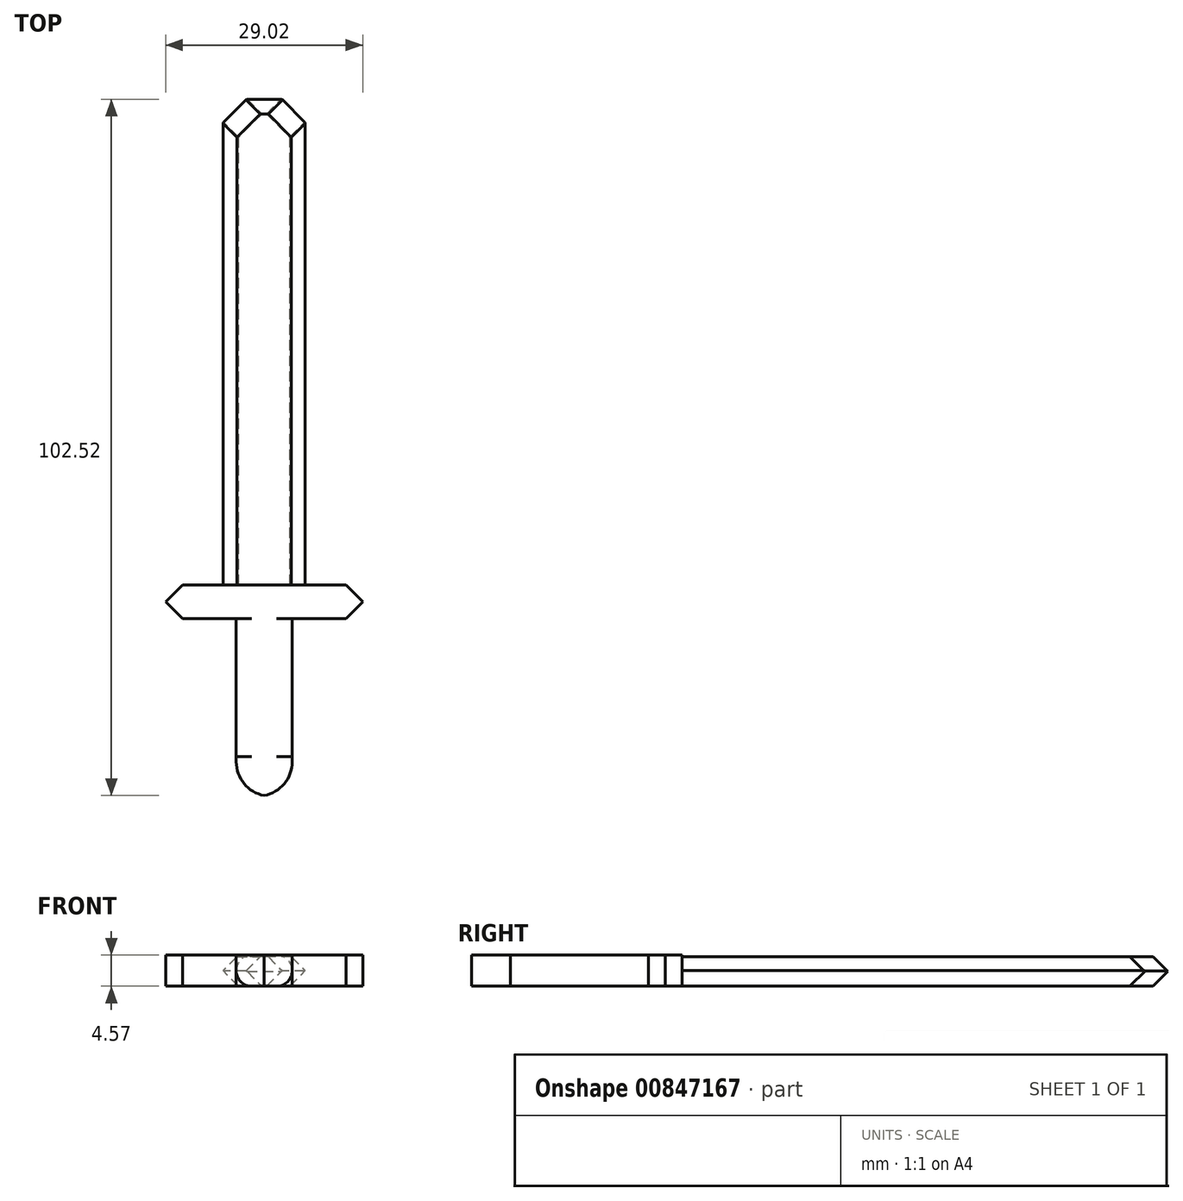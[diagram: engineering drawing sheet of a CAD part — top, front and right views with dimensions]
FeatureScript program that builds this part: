
annotation { "Feature Type Name" : "Feature", "Feature Type Description" : "" }
export const myFeature = defineFeature(function(context is Context, id is Id, definition is map)
    precondition{}
    {
        {
            var Q0;
            Q0=qCreatedBy(makeId("Top.planeOp"),FACE);
            var sketch = newSketch(context, id + "F0", { "sketchPlane" : qUnion([Q0])});
            skLineSegment(sketch, "E0.bottom", {"start": v(6.04, 35.82) * mm, "end": v(-6.04, 35.82) * mm});
            skLineSegment(sketch, "E0.top", {"start": v(6.04, -35.82) * mm, "end": v(-6.04, -35.82) * mm});
            skLineSegment(sketch, "E0.left", {"start": v(6.04, 35.82) * mm, "end": v(6.04, -35.82) * mm});
            skLineSegment(sketch, "E0.right", {"start": v(-6.04, 35.82) * mm, "end": v(-6.04, -35.82) * mm});
            skPoint(sketch, "E0.middle", {"position": v(0, 0) * mm});
            skSolve(sketch);
        }
        {
            var Q0;
            Q0=makeQuery(id+"F0.imprint","IMPRINT",FACE,{"disambiguationData":[TD([[makeQuery(id+"F0.imprint","IMPRINT",EDGE,{"derivedFrom":sQuery(id+"F0.wireOp",EDGE,"E0.bottom")}),1.0]])]});
            extrude(context, id + "F1", {"entities" : qUnion([Q0]), "depth" : 4.32 * mm, "offsetDistance" : 25.4 * mm});
        }
        {
            var Q0;
            Q0=makeQuery(id+"F1.opExtrude","CAP_EDGE",EDGE,{"disambiguationData":[OSD([sQuery(id+"F0.wireOp",EDGE,"E0.left")])],"isStart":false});
            chamfer(context, id + "F2", {"entities" : qUnion([Q0]), "width" : 2.03 * mm, "tangentPropagation" : true});
        }
        {
            var Q0;
            Q0=makeQuery(id+"F1.opExtrude","CAP_EDGE",EDGE,{"disambiguationData":[OSD([sQuery(id+"F0.wireOp",EDGE,"E0.left")])],"isStart":true});
            chamfer(context, id + "F3", {"entities" : qUnion([Q0]), "width" : 2.3 * mm, "tangentPropagation" : true});
        }
        {
            var Q0;
            Q0=makeQuery(id+"F1.opExtrude","CAP_EDGE",EDGE,{"disambiguationData":[OSD([sQuery(id+"F0.wireOp",EDGE,"E0.right")])],"isStart":false});
            chamfer(context, id + "F4", {"entities" : qUnion([Q0]), "width" : 2.03 * mm, "tangentPropagation" : true});
        }
        {
            var Q0;
            Q0=makeQuery(id+"F1.opExtrude","CAP_EDGE",EDGE,{"disambiguationData":[OSD([sQuery(id+"F0.wireOp",EDGE,"E0.right")])],"isStart":true});
            chamfer(context, id + "F5", {"entities" : qUnion([Q0]), "width" : 2.3 * mm, "tangentPropagation" : true});
        }
        {
            var Q0;
            Q0=makeQuery(id+"F1.opExtrude","CAP_EDGE",EDGE,{"disambiguationData":[OSD([sQuery(id+"F0.wireOp",EDGE,"E0.bottom")])],"isStart":false});
            chamfer(context, id + "F6", {"entities" : qUnion([Q0]), "width" : 2.3 * mm, "tangentPropagation" : true});
        }
        {
            var Q0;
            Q0=makeQuery(id+"F1.opExtrude","CAP_EDGE",EDGE,{"disambiguationData":[OSD([sQuery(id+"F0.wireOp",EDGE,"E0.bottom")])],"isStart":true});
            chamfer(context, id + "F7", {"entities" : qUnion([Q0]), "width" : 2.3 * mm, "tangentPropagation" : true});
        }
        {
            var Q0;
            Q0=makeQuery(id+"F6.opChamfer","BLEND_EDGE",EDGE,{"blendedFrom":[makeQuery(id+"F1.opExtrude","CAP_EDGE",EDGE,{"disambiguationData":[OSD([sQuery(id+"F0.wireOp",EDGE,"E0.bottom")])],"isStart":false}),makeQuery(id+"F4.opChamfer","BLEND_FACE",FACE,{"disambiguationData":[OSD([sQuery(id+"F0.wireOp",EDGE,"E0.right")])]})],"blendedInto":[makeQuery(id+"F4.opChamfer","BLEND_FACE",FACE,{"disambiguationData":[OSD([sQuery(id+"F0.wireOp",EDGE,"E0.right")])]})]});
            chamfer(context, id + "F8", {"entities" : qUnion([Q0]), "width" : 4.83 * mm, "tangentPropagation" : true});
        }
        {
            var Q0;
            Q0=makeQuery(id+"F7.opChamfer","BLEND_EDGE",EDGE,{"blendedFrom":[makeQuery(id+"F1.opExtrude","CAP_EDGE",EDGE,{"disambiguationData":[OSD([sQuery(id+"F0.wireOp",EDGE,"E0.bottom")])],"isStart":true}),makeQuery(id+"F5.opChamfer","BLEND_FACE",FACE,{"disambiguationData":[OSD([sQuery(id+"F0.wireOp",EDGE,"E0.right")])]})],"blendedInto":[makeQuery(id+"F5.opChamfer","BLEND_FACE",FACE,{"disambiguationData":[OSD([sQuery(id+"F0.wireOp",EDGE,"E0.right")])]})]});
            chamfer(context, id + "F9", {"entities" : qUnion([Q0]), "width" : 4.83 * mm, "tangentPropagation" : true});
        }
        {
            var Q0;
            Q0=makeQuery(id+"F6.opChamfer","BLEND_EDGE",EDGE,{"blendedFrom":[makeQuery(id+"F1.opExtrude","CAP_EDGE",EDGE,{"disambiguationData":[OSD([sQuery(id+"F0.wireOp",EDGE,"E0.bottom")])],"isStart":false}),makeQuery(id+"F2.opChamfer","BLEND_FACE",FACE,{"disambiguationData":[OSD([sQuery(id+"F0.wireOp",EDGE,"E0.left")])]})],"blendedInto":[makeQuery(id+"F2.opChamfer","BLEND_FACE",FACE,{"disambiguationData":[OSD([sQuery(id+"F0.wireOp",EDGE,"E0.left")])]})]});
            chamfer(context, id + "F10", {"entities" : qUnion([Q0]), "width" : 4.83 * mm, "tangentPropagation" : true});
        }
        {
            var Q0;
            Q0=makeQuery(id+"F7.opChamfer","BLEND_EDGE",EDGE,{"blendedFrom":[makeQuery(id+"F1.opExtrude","CAP_EDGE",EDGE,{"disambiguationData":[OSD([sQuery(id+"F0.wireOp",EDGE,"E0.bottom")])],"isStart":true}),makeQuery(id+"F3.opChamfer","BLEND_FACE",FACE,{"disambiguationData":[OSD([sQuery(id+"F0.wireOp",EDGE,"E0.left")])]})],"blendedInto":[makeQuery(id+"F3.opChamfer","BLEND_FACE",FACE,{"disambiguationData":[OSD([sQuery(id+"F0.wireOp",EDGE,"E0.left")])]})]});
            chamfer(context, id + "F11", {"entities" : qUnion([Q0]), "width" : 4.83 * mm, "tangentPropagation" : true});
        }
        {
            var Q0;
            Q0=makeQuery(id+"F1.opExtrude","SWEPT_FACE",FACE,{"disambiguationData":[OSD([sQuery(id+"F0.wireOp",EDGE,"E0.top")])]});
            var sketch = newSketch(context, id + "F12", { "sketchPlane" : qUnion([Q0])});
            skLineSegment(sketch, "E1.bottom", {"start": v(14.57, 0) * mm, "end": v(-14.57, 0) * mm});
            skLineSegment(sketch, "E1.top", {"start": v(14.57, 4.57) * mm, "end": v(-14.57, 4.57) * mm});
            skLineSegment(sketch, "E1.left", {"start": v(14.57, 0) * mm, "end": v(14.57, 4.57) * mm});
            skLineSegment(sketch, "E1.right", {"start": v(-14.57, 0) * mm, "end": v(-14.57, 4.57) * mm});
            skPoint(sketch, "E1.middle", {"position": v(0, 2.29) * mm});
            skSolve(sketch);
        }
        {
            var Q0;
            Q0=makeQuery(id+"F12.imprint","IMPRINT",FACE,{"disambiguationData":[TD([[makeQuery(id+"F12.imprint","IMPRINT",EDGE,{"derivedFrom":sQuery(id+"F12.wireOp",EDGE,"E1.top")}),1.0]])]});
            var Q1;
            {var subQ1=sQuery(id+"F0.wireOp",EDGE,"E0.top");Q1=makeQuery(id+"F12.imprint","IMPRINT",FACE,{"disambiguationData":[TD([[makeQuery(id+"F12.imprint","IMPRINT",EDGE,{"derivedFrom":makeQuery(id+"F1.opExtrude","CAP_EDGE",EDGE,{"disambiguationData":[OSD([subQ1])],"isStart":false})}),1.0]])]});}
            extrude(context, id + "F13", {"entities" : qUnion([Q0, Q1]), "operationType" : NewBodyOperationType.ADD, "depth" : 4.97 * mm, "offsetDistance" : 25.4 * mm});
        }
        {
            var Q0;
            Q0=makeQuery(id+"F13.opExtrude","CAP_EDGE",EDGE,{"disambiguationData":[OSD([sQuery(id+"F12.wireOp",EDGE,"E1.left")])],"isStart":true});
            var Q1;
            Q1=makeQuery(id+"F13.opExtrude","CAP_EDGE",EDGE,{"disambiguationData":[OSD([sQuery(id+"F12.wireOp",EDGE,"E1.left")])],"isStart":false});
            var Q2;
            Q2=makeQuery(id+"F13.opExtrude","CAP_EDGE",EDGE,{"disambiguationData":[OSD([sQuery(id+"F12.wireOp",EDGE,"E1.right")])],"isStart":true});
            var Q3;
            Q3=makeQuery(id+"F13.opExtrude","CAP_EDGE",EDGE,{"disambiguationData":[OSD([sQuery(id+"F12.wireOp",EDGE,"E1.right")])],"isStart":false});
            chamfer(context, id + "F14", {"entities" : qUnion([Q0, Q1, Q2, Q3]), "width" : 2.54 * mm, "tangentPropagation" : true});
        }
        {
            var Q0;
            Q0=makeQuery(id+"F13.opExtrude","CAP_FACE",FACE,{"disambiguationData":[OSD([sQuery(id+"F12.wireOp",EDGE,"E1.bottom"),sQuery(id+"F12.wireOp",EDGE,"E1.top"),sQuery(id+"F12.wireOp",EDGE,"E1.left"),sQuery(id+"F12.wireOp",EDGE,"E1.right")])],"isStart":false});
            var sketch = newSketch(context, id + "F15", { "sketchPlane" : qUnion([Q0])});
            skLineSegment(sketch, "E2.bottom", {"start": v(4.12, 0) * mm, "end": v(-4.12, 0) * mm});
            skLineSegment(sketch, "E2.top", {"start": v(4.12, 4.57) * mm, "end": v(-4.12, 4.57) * mm});
            skLineSegment(sketch, "E2.left", {"start": v(4.12, 0) * mm, "end": v(4.12, 4.57) * mm});
            skLineSegment(sketch, "E2.right", {"start": v(-4.12, 0) * mm, "end": v(-4.12, 4.57) * mm});
            skPoint(sketch, "E2.middle", {"position": v(0, 2.29) * mm});
            skPoint(sketch, "E2.middle.positionSnap0", {"position": v(12.03, 2.29) * mm});
            skPoint(sketch, "E2.centerSnap0", {"position": v(12.03, 2.29) * mm});
            skSolve(sketch);
        }
        {
            var Q0;
            Q0=makeQuery(id+"F15.imprint","IMPRINT",FACE,{"disambiguationData":[TD([[makeQuery(id+"F15.imprint","IMPRINT",EDGE,{"derivedFrom":sQuery(id+"F15.wireOp",EDGE,"E2.bottom")}),-1.0]])]});
            extrude(context, id + "F16", {"entities" : qUnion([Q0]), "operationType" : NewBodyOperationType.ADD, "depth" : 20.32 * mm, "offsetDistance" : 25.4 * mm});
        }
        {
            var Q0;
            Q0=makeQuery(id+"F16.opExtrude","SWEPT_EDGE",EDGE,{"disambiguationData":[OSD([sQuery(id+"F12.wireOp",EDGE,"E1.top"),sQuery(id+"F15.wireOp",EDGE,"E2.top"),sQuery(id+"F15.wireOp",EDGE,"E2.left")])]});
            var Q1;
            Q1=makeQuery(id+"F16.opExtrude","SWEPT_EDGE",EDGE,{"disambiguationData":[OSD([sQuery(id+"F12.wireOp",EDGE,"E1.bottom"),sQuery(id+"F15.wireOp",EDGE,"E2.bottom"),sQuery(id+"F15.wireOp",EDGE,"E2.left")])]});
            var Q2;
            Q2=makeQuery(id+"F16.opExtrude","SWEPT_EDGE",EDGE,{"disambiguationData":[OSD([sQuery(id+"F12.wireOp",EDGE,"E1.top"),sQuery(id+"F15.wireOp",EDGE,"E2.top"),sQuery(id+"F15.wireOp",EDGE,"E2.right")])]});
            var Q3;
            Q3=makeQuery(id+"F16.opExtrude","SWEPT_EDGE",EDGE,{"disambiguationData":[OSD([sQuery(id+"F12.wireOp",EDGE,"E1.bottom"),sQuery(id+"F15.wireOp",EDGE,"E2.bottom"),sQuery(id+"F15.wireOp",EDGE,"E2.right")])]});
            fillet(context, id + "F17", {"entities" : qUnion([Q0, Q1, Q2, Q3]), "radius" : 2.3 * mm, "tangentPropagation" : true, "allowEdgeOverflow" : false});
        }
        {
            var Q0;
            Q0=makeQuery(id+"F16.opExtrude","CAP_FACE",FACE,{"disambiguationData":[OSD([sQuery(id+"F15.wireOp",EDGE,"E2.bottom"),sQuery(id+"F15.wireOp",EDGE,"E2.top"),sQuery(id+"F15.wireOp",EDGE,"E2.left"),sQuery(id+"F15.wireOp",EDGE,"E2.right")])],"isStart":false});
            var sketch = newSketch(context, id + "F18", { "sketchPlane" : qUnion([Q0])});
            skLineSegment(sketch, "E3.bottom", {"start": v(4.12, 0) * mm, "end": v(-4.12, 0) * mm});
            skLineSegment(sketch, "E3.top", {"start": v(4.12, 4.57) * mm, "end": v(-4.12, 4.57) * mm});
            skLineSegment(sketch, "E3.left", {"start": v(4.12, 0) * mm, "end": v(4.12, 4.57) * mm});
            skLineSegment(sketch, "E3.right", {"start": v(-4.12, 0) * mm, "end": v(-4.12, 4.57) * mm});
            skPoint(sketch, "E3.middle", {"position": v(0, 2.29) * mm});
            skPoint(sketch, "E3.middle.positionSnap0", {"position": v(4.12, 2.29) * mm});
            skPoint(sketch, "E3.cornerSnap0", {"position": v(4.12, 2.29) * mm});
            skPoint(sketch, "E3.centerSnap0", {"position": v(4.12, 2.29) * mm});
            skSolve(sketch);
        }
        {
            var Q0;
            {var subQ0=sQuery(id+"F18.wireOp",EDGE,"E3.bottom");var subQ1=sQuery(id+"F15.wireOp",EDGE,"E2.right");var subQ2=sQuery(id+"F15.wireOp",EDGE,"E2.left");var subQ3=sQuery(id+"F15.wireOp",EDGE,"E2.bottom");var subQ4=makeQuery(id+"F16.opExtrude","CAP_FACE",FACE,{"disambiguationData":[OSD([subQ3,sQuery(id+"F15.wireOp",EDGE,"E2.top"),subQ2,subQ1])],"isStart":false});var subQ5=sQuery(id+"F12.wireOp",EDGE,"E1.bottom");var subQ6=makeQuery(id+"F17.opFillet","BLEND_EDGE",EDGE,{"blendedFrom":[makeQuery(id+"F16.opExtrude","SWEPT_EDGE",EDGE,{"disambiguationData":[OSD([subQ5,subQ3,subQ2])]}),subQ4],"blendedInto":[subQ4]});var subQ7=makeQuery(id+"F18.imprint","INTERSECT",VERTEX,{"derivedFrom":[subQ6,subQ0]});Q0=makeQuery(id+"F18.imprint","IMPRINT",FACE,{"disambiguationData":[TD([[makeQuery(id+"F18.imprint","IMPRINT",EDGE,{"disambiguationData":[TD([[subQ7,-1.0]])],"derivedFrom":subQ0}),-1.0]])]});}
            var Q1;
            {var subQ0=sQuery(id+"F18.wireOp",EDGE,"E3.bottom");var subQ5=sQuery(id+"F18.wireOp",EDGE,"E3.left");var subQ6=makeQuery(id+"F18.imprint","INTERSECT",VERTEX,{"derivedFrom":[subQ0,subQ5]});Q1=makeQuery(id+"F18.imprint","IMPRINT",FACE,{"disambiguationData":[TD([[makeQuery(id+"F18.imprint","IMPRINT",EDGE,{"disambiguationData":[TD([[subQ6,-1.0]])],"derivedFrom":subQ0}),-1.0]])]});}
            var Q2;
            {var subQ0=sQuery(id+"F18.wireOp",EDGE,"E3.top");var subQ5=sQuery(id+"F18.wireOp",EDGE,"E3.right");var subQ6=makeQuery(id+"F18.imprint","INTERSECT",VERTEX,{"derivedFrom":[subQ0,subQ5]});Q2=makeQuery(id+"F18.imprint","IMPRINT",FACE,{"disambiguationData":[TD([[makeQuery(id+"F18.imprint","IMPRINT",EDGE,{"disambiguationData":[TD([[subQ6,1.0]])],"derivedFrom":subQ0}),1.0]])]});}
            var Q3;
            {var subQ0=sQuery(id+"F18.wireOp",EDGE,"E3.top");var subQ5=sQuery(id+"F18.wireOp",EDGE,"E3.left");var subQ6=makeQuery(id+"F18.imprint","INTERSECT",VERTEX,{"derivedFrom":[subQ0,subQ5]});Q3=makeQuery(id+"F18.imprint","IMPRINT",FACE,{"disambiguationData":[TD([[makeQuery(id+"F18.imprint","IMPRINT",EDGE,{"disambiguationData":[TD([[subQ6,-1.0]])],"derivedFrom":subQ0}),1.0]])]});}
            var Q4;
            {var subQ0=sQuery(id+"F18.wireOp",EDGE,"E3.bottom");var subQ5=sQuery(id+"F18.wireOp",EDGE,"E3.right");var subQ6=makeQuery(id+"F18.imprint","INTERSECT",VERTEX,{"derivedFrom":[subQ0,subQ5]});Q4=makeQuery(id+"F18.imprint","IMPRINT",FACE,{"disambiguationData":[TD([[makeQuery(id+"F18.imprint","IMPRINT",EDGE,{"disambiguationData":[TD([[subQ6,1.0]])],"derivedFrom":subQ0}),-1.0]])]});}
            extrude(context, id + "F19", {"entities" : qUnion([Q0, Q1, Q2, Q3, Q4]), "operationType" : NewBodyOperationType.ADD, "depth" : 5.8 * mm, "offsetDistance" : 25.4 * mm});
        }
        {
            var Q0;
            Q0=makeQuery(id+"F19.opExtrude","CAP_EDGE",EDGE,{"disambiguationData":[OSD([sQuery(id+"F18.wireOp",EDGE,"E3.left")])],"isStart":false});
            var Q1;
            Q1=makeQuery(id+"F19.opExtrude","CAP_EDGE",EDGE,{"disambiguationData":[OSD([sQuery(id+"F18.wireOp",EDGE,"E3.right")])],"isStart":false});
            fillet(context, id + "F20", {"entities" : qUnion([Q0, Q1]), "radius" : 5.08 * mm, "tangentPropagation" : true, "allowEdgeOverflow" : false});
        }
    });
